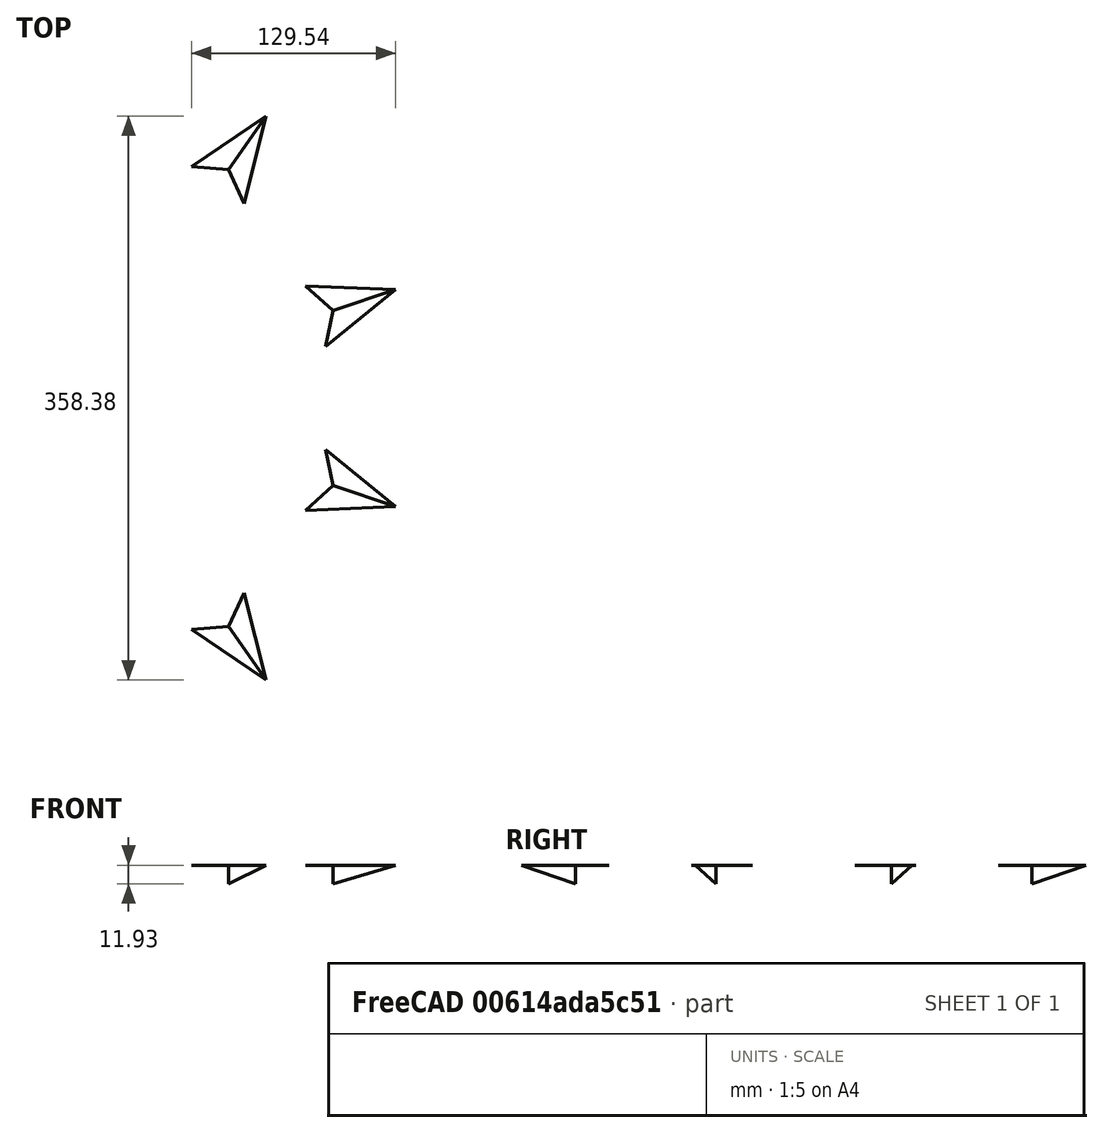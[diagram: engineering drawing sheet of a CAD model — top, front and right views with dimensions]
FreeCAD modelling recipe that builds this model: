
FCSTD DOCUMENT  (FreeCAD 1.1R38827 (Git))
Label: composit_stand3_basin_holder_main
License: All rights reserved
LicenseURL: http://en.wikipedia.org/wiki/All_rights_reserved
objects: Part::FeaturePython×2, Sketcher::SketchObject×1
note: 4 computed .brp shape members not serialized (recipe doc carries the construction recipe); baked Part::Feature solids carry a one-line shape summary decoded from their .brp
EXTERNAL_REF file=../basin_big.FCStd obj=Spreadsheet

FEATURE [Sketcher::SketchObject] Sketch  label="main_sketch"
  ArcFitTolerance = 0
  FullyConstrained = true
  MakeInternals = false
  expr: .Constraints.min_r = <<basin_big>>#<<Properties>>.bottom_d / 2 + 10 mm
  sketch-geometry (5):
    g0: ArcOfCircle CenterX=0 CenterY=0 CenterZ=0 NormalX=0 NormalY=0 NormalZ=1 AngleXU=0 Radius=170 StartAngle=0 EndAngle=0.966832
    g1: ArcOfCircle CenterX=0 CenterY=0 CenterZ=0 NormalX=0 NormalY=0 NormalZ=1 AngleXU=0 Radius=185 StartAngle=0 EndAngle=1.0335
    g2: LineSegment [constr] StartX=0 StartY=0 StartZ=0 EndX=91.2414 EndY=158.035 EndZ=0
    g3: ArcOfCircle CenterX=105.063 CenterY=152.272 CenterZ=0 NormalX=0 NormalY=0 NormalZ=1 AngleXU=0 Radius=15 StartAngle=2.77221 EndAngle=4.10842
    g4: ArcOfCircle CenterX=93.4065 CenterY=156.785 CenterZ=0 NormalX=0 NormalY=0 NormalZ=1 AngleXU=0 Radius=2.5 StartAngle=1.0335 EndAngle=2.77221
  constraints (15):
    c: Coincident(g0,g-1)
    c: PointOnObject(g0,g-1)
    c: Coincident(g1,g0)
    c: PointOnObject(g1,g-1)
    c: DistanceX(g0) = 170  'min_r'
    c: DistanceX(g0,g1) = 15
    c: Coincident(g2,g0)
    c: Angle(g2) = 1.0472
    c: DistanceX(g1) = 185  'max_r'
    c: Tangent(g1,g4) = -1.5708
    c: Tangent(g3,g4) = -1.5708
    c: Radius(g4) = 2.5
    c: PointOnObject(g3,g1)
    c: Tangent(g2,g4) = 1.5708
    c: Tangent(g3,g0) = 1.5708
FEATURE [Part::FeaturePython] PolarArray  # WARN: FeaturePython — macro-defined, semantics opaque (R4)
  Alignment = 0
  AttacherType = Attacher::AttachEngine3D
  CellStart = A1
  Count = 4
  DistributionLaw = 0
  EndInclusive = true
  ExposePlacement = false
  FlipX = false
  FlipZ = false
  GeneratorMode = 0
  MarkerShape = 1
  MarkerSize = 0
  NumElements = 4
  OrientMode = 2
  Radius = 177
  Reverse = false
  SpanEnd = 55
  SpanStart = -55
  Step = 36.6667
  Type = lattice2PolarArray2.PolarArray
  UseArcRadius = false
  UseArcRange = 0
  VSGVersion = 1
  Values = -55.0 | -18.333333333333336 | 18.33333333333333 | 55.0
  ValuesSource = 2
  isLattice = 1
  expr: Radius = <<main_sketch>>.Constraints.min_r + 7 mm
  expr: SpanEnd = -SpanStart
FEATURE [Part::FeaturePython] Join  label="holes"  # WARN: FeaturePython — macro-defined, semantics opaque (R4)
  ExposePlacement = false
  Interleave = false
  Links = -> [PolarArray]
  MarkerShape = 1
  MarkerSize = 0
  NumElements = 4
  Type = lattice2JoinArrays.JoinArrays
  isLattice = 1
